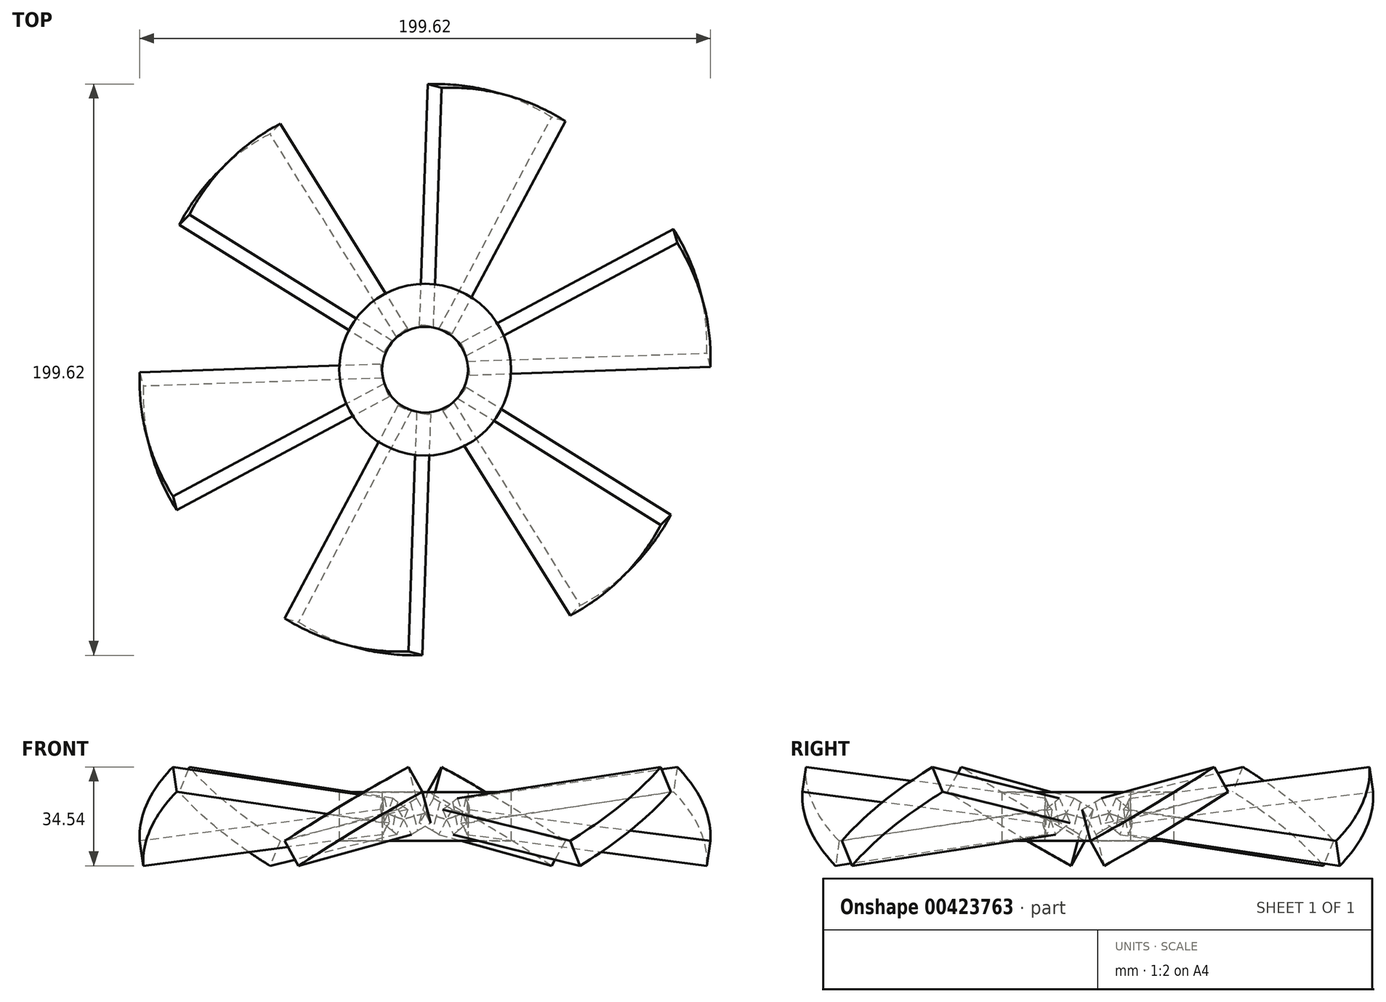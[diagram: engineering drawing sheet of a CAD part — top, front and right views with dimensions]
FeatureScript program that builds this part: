
annotation { "Feature Type Name" : "Feature", "Feature Type Description" : "" }
export const myFeature = defineFeature(function(context is Context, id is Id, definition is map)
    precondition{}
    {
        {
            var Q0;
            Q0=qCreatedBy(makeId("Top.planeOp"),FACE);
            var sketch = newSketch(context, id + "F0", { "sketchPlane" : qUnion([Q0])});
            skCircle(sketch, "E0", {"center": v(0, 0) * mm, "radius": 15 * mm});
            skCircle(sketch, "E1", {"center": v(0, 0) * mm, "radius": 30 * mm});
            skArc(sketch, "E2", {"start": v(100, 0) * mm, "mid": v(96.6, 25.88) * mm, "end": v(86.6, 50) * mm});
            skLineSegment(sketch, "E3", {"start": v(30, 0) * mm, "end": v(100, 0) * mm});
            skLineSegment(sketch, "E4", {"start": v(0, 0) * mm, "end": v(86.6, 50) * mm});
            skLineSegment(sketch, "E5", {"start": v(30, 0) * mm, "end": v(0, 0) * mm});
            skLineSegment(sketch, "E6", {"start": v(0, 0) * mm, "end": v(96.6, 25.88) * mm});
            skSolve(sketch);
        }
        {
            var Q0;
            {var subQ4=sQuery(id+"F0.wireOp",EDGE,"E2");Q0=makeQuery(id+"F0.imprint","IMPRINT",FACE,{"disambiguationData":[TD([[makeQuery(id+"F0.imprint","IMPRINT",EDGE,{"derivedFrom":subQ4}),1.0]])]});}
            var Q1;
            {var subQ0=sQuery(id+"F0.wireOp",EDGE,"E6");var subQ1=sQuery(id+"F0.wireOp",EDGE,"E0");var subQ2=makeQuery(id+"F0.imprint","INTERSECT",VERTEX,{"derivedFrom":[subQ1,subQ0]});Q1=makeQuery(id+"F0.imprint","IMPRINT",FACE,{"disambiguationData":[TD([[makeQuery(id+"F0.imprint","IMPRINT",EDGE,{"disambiguationData":[TD([[subQ2,1.0]])],"derivedFrom":subQ1}),-1.0]])]});}
            var Q2;
            {var subQ0=sQuery(id+"F0.wireOp",EDGE,"E6");var subQ1=sQuery(id+"F0.wireOp",EDGE,"E0");var subQ2=makeQuery(id+"F0.imprint","INTERSECT",VERTEX,{"derivedFrom":[subQ1,subQ0]});Q2=makeQuery(id+"F0.imprint","IMPRINT",FACE,{"disambiguationData":[TD([[makeQuery(id+"F0.imprint","IMPRINT",EDGE,{"disambiguationData":[TD([[subQ2,-1.0]])],"derivedFrom":subQ1}),-1.0]])]});}
            extrude(context, id + "F1", {"entities" : qUnion([Q0, Q1, Q2]), "endBound" : BoundingType.SYMMETRIC, "depth" : 10 * mm});
        }
        {
            var Q0;
            Q0=makeQuery(id+"F1.opExtrude","SWEPT_BODY",BODY,{"disambiguationData":[OSD([sQuery(id+"F0.wireOp",EDGE,"E0"),sQuery(id+"F0.wireOp",EDGE,"E2"),sQuery(id+"F0.wireOp",EDGE,"E3"),sQuery(id+"F0.wireOp",EDGE,"E4"),sQuery(id+"F0.wireOp",EDGE,"E5")])]});
            var Q1;
            Q1=sQuery(id+"F0.wireOp",EDGE,"E6");
            transform(context, id + "F2", {"entities" : qUnion([Q0]), "transformType" : TransformType.ROTATION, "transformAxis" : qUnion([Q1]), "angle" : 30 * degree, "makeCopy" : false});
        }
        {
            var Q0;
            Q0=qCreatedBy(makeId("Front.planeOp"),FACE);
            var sketch = newSketch(context, id + "F3", { "sketchPlane" : qUnion([Q0])});
            skLineSegment(sketch, "E7", {"start": v(0, 0) * mm, "end": v(0, 71.27) * mm});
            skSolve(sketch);
        }
        {
            var Q0;
            Q0=makeQuery(id+"F1.opExtrude","SWEPT_BODY",BODY,{"disambiguationData":[OSD([sQuery(id+"F0.wireOp",EDGE,"E0"),sQuery(id+"F0.wireOp",EDGE,"E2"),sQuery(id+"F0.wireOp",EDGE,"E3"),sQuery(id+"F0.wireOp",EDGE,"E4"),sQuery(id+"F0.wireOp",EDGE,"E5")])]});
            var Q1;
            Q1=sQuery(id+"F3.wireOp",EDGE,"E7");
            circularPattern(context, id + "F4", {"entities" : qUnion([Q0]), "axis" : qUnion([Q1]), "angle" : 360 * degree, "instanceCount" : 6, "equalSpace" : true});
        }
        {
            var Q0;
            {var subQ0=sQuery(id+"F0.wireOp",EDGE,"E4");var subQ1=sQuery(id+"F0.wireOp",EDGE,"E0");var subQ2=makeQuery(id+"F0.imprint","INTERSECT",VERTEX,{"derivedFrom":[subQ1,subQ0]});Q0=makeQuery(id+"F0.imprint","IMPRINT",FACE,{"disambiguationData":[TD([[makeQuery(id+"F0.imprint","IMPRINT",EDGE,{"disambiguationData":[TD([[subQ2,-1.0]])],"derivedFrom":subQ1}),-1.0]])]});}
            var Q1;
            {var subQ0=sQuery(id+"F0.wireOp",EDGE,"E4");var subQ1=sQuery(id+"F0.wireOp",EDGE,"E0");var subQ2=makeQuery(id+"F0.imprint","INTERSECT",VERTEX,{"derivedFrom":[subQ1,subQ0]});Q1=makeQuery(id+"F0.imprint","IMPRINT",FACE,{"disambiguationData":[TD([[makeQuery(id+"F0.imprint","IMPRINT",EDGE,{"disambiguationData":[TD([[subQ2,1.0]])],"derivedFrom":subQ1}),-1.0]])]});}
            var Q2;
            {var subQ0=sQuery(id+"F0.wireOp",EDGE,"E6");var subQ1=sQuery(id+"F0.wireOp",EDGE,"E0");var subQ2=makeQuery(id+"F0.imprint","INTERSECT",VERTEX,{"derivedFrom":[subQ1,subQ0]});Q2=makeQuery(id+"F0.imprint","IMPRINT",FACE,{"disambiguationData":[TD([[makeQuery(id+"F0.imprint","IMPRINT",EDGE,{"disambiguationData":[TD([[subQ2,1.0]])],"derivedFrom":subQ1}),-1.0]])]});}
            extrude(context, id + "F5", {"entities" : qUnion([Q0, Q1, Q2]), "endBound" : BoundingType.SYMMETRIC, "depth" : 17 * mm});
        }
        {
            var Q0;
            {var subQ0=sQuery(id+"F0.wireOp",EDGE,"E5");var subQ1=sQuery(id+"F0.wireOp",EDGE,"E0");var subQ2=makeQuery(id+"F0.imprint","INTERSECT",VERTEX,{"derivedFrom":[subQ1,subQ0]});Q0=makeQuery(id+"F0.imprint","IMPRINT",FACE,{"disambiguationData":[TD([[makeQuery(id+"F0.imprint","IMPRINT",EDGE,{"disambiguationData":[TD([[subQ2,1.0]])],"derivedFrom":subQ1}),1.0]])]});}
            var Q1;
            {var subQ0=sQuery(id+"F0.wireOp",EDGE,"E6");var subQ1=sQuery(id+"F0.wireOp",EDGE,"E0");var subQ2=makeQuery(id+"F0.imprint","INTERSECT",VERTEX,{"derivedFrom":[subQ1,subQ0]});Q1=makeQuery(id+"F0.imprint","IMPRINT",FACE,{"disambiguationData":[TD([[makeQuery(id+"F0.imprint","IMPRINT",EDGE,{"disambiguationData":[TD([[subQ2,-1.0]])],"derivedFrom":subQ1}),1.0]])]});}
            var Q2;
            {var subQ0=sQuery(id+"F0.wireOp",EDGE,"E6");var subQ1=sQuery(id+"F0.wireOp",EDGE,"E0");var subQ2=makeQuery(id+"F0.imprint","INTERSECT",VERTEX,{"derivedFrom":[subQ1,subQ0]});Q2=makeQuery(id+"F0.imprint","IMPRINT",FACE,{"disambiguationData":[TD([[makeQuery(id+"F0.imprint","IMPRINT",EDGE,{"disambiguationData":[TD([[subQ2,1.0]])],"derivedFrom":subQ1}),1.0]])]});}
            extrude(context, id + "F6", {"entities" : qUnion([Q0, Q1, Q2]), "operationType" : NewBodyOperationType.REMOVE, "endBound" : BoundingType.SYMMETRIC, "depth" : 100 * mm});
        }
    });
